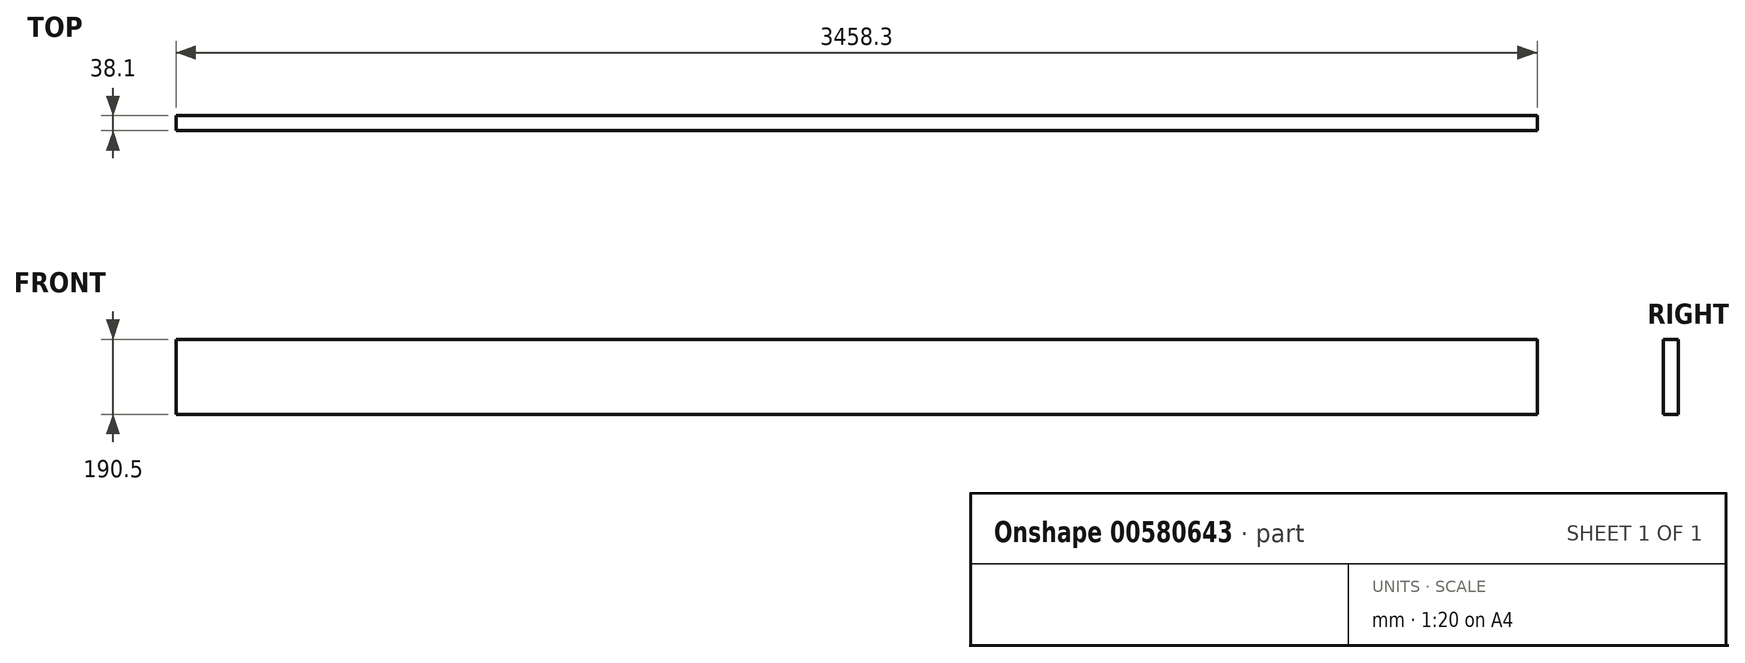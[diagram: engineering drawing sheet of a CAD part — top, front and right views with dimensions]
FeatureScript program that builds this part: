
annotation { "Feature Type Name" : "Feature", "Feature Type Description" : "" }
export const myFeature = defineFeature(function(context is Context, id is Id, definition is map)
    precondition{}
    {
        {
            var Q0;
            Q0=qCreatedBy(makeId("Top.planeOp"),FACE);
            var sketch = newSketch(context, id + "F0", { "sketchPlane" : qUnion([Q0])});
            skLineSegment(sketch, "E0.bottom", {"start": v(1729.15, -19.05) * mm, "end": v(-1729.15, -19.05) * mm});
            skLineSegment(sketch, "E0.top", {"start": v(1729.15, 19.05) * mm, "end": v(-1729.15, 19.05) * mm});
            skLineSegment(sketch, "E0.left", {"start": v(1729.15, -19.05) * mm, "end": v(1729.15, 19.05) * mm});
            skLineSegment(sketch, "E0.right", {"start": v(-1729.15, -19.05) * mm, "end": v(-1729.15, 19.05) * mm});
            skPoint(sketch, "E0.middle", {"position": v(0, 0) * mm});
            skSolve(sketch);
        }
        {
            var Q0;
            Q0=makeQuery(id+"F0.imprint","IMPRINT",FACE,{"disambiguationData":[TD([[makeQuery(id+"F0.imprint","IMPRINT",EDGE,{"derivedFrom":sQuery(id+"F0.wireOp",EDGE,"E0.bottom")}),-1.0]])]});
            extrude(context, id + "F1", {"entities" : qUnion([Q0]), "depth" : 190.5 * mm, "offsetDistance" : 25.4 * mm});
        }
    });
